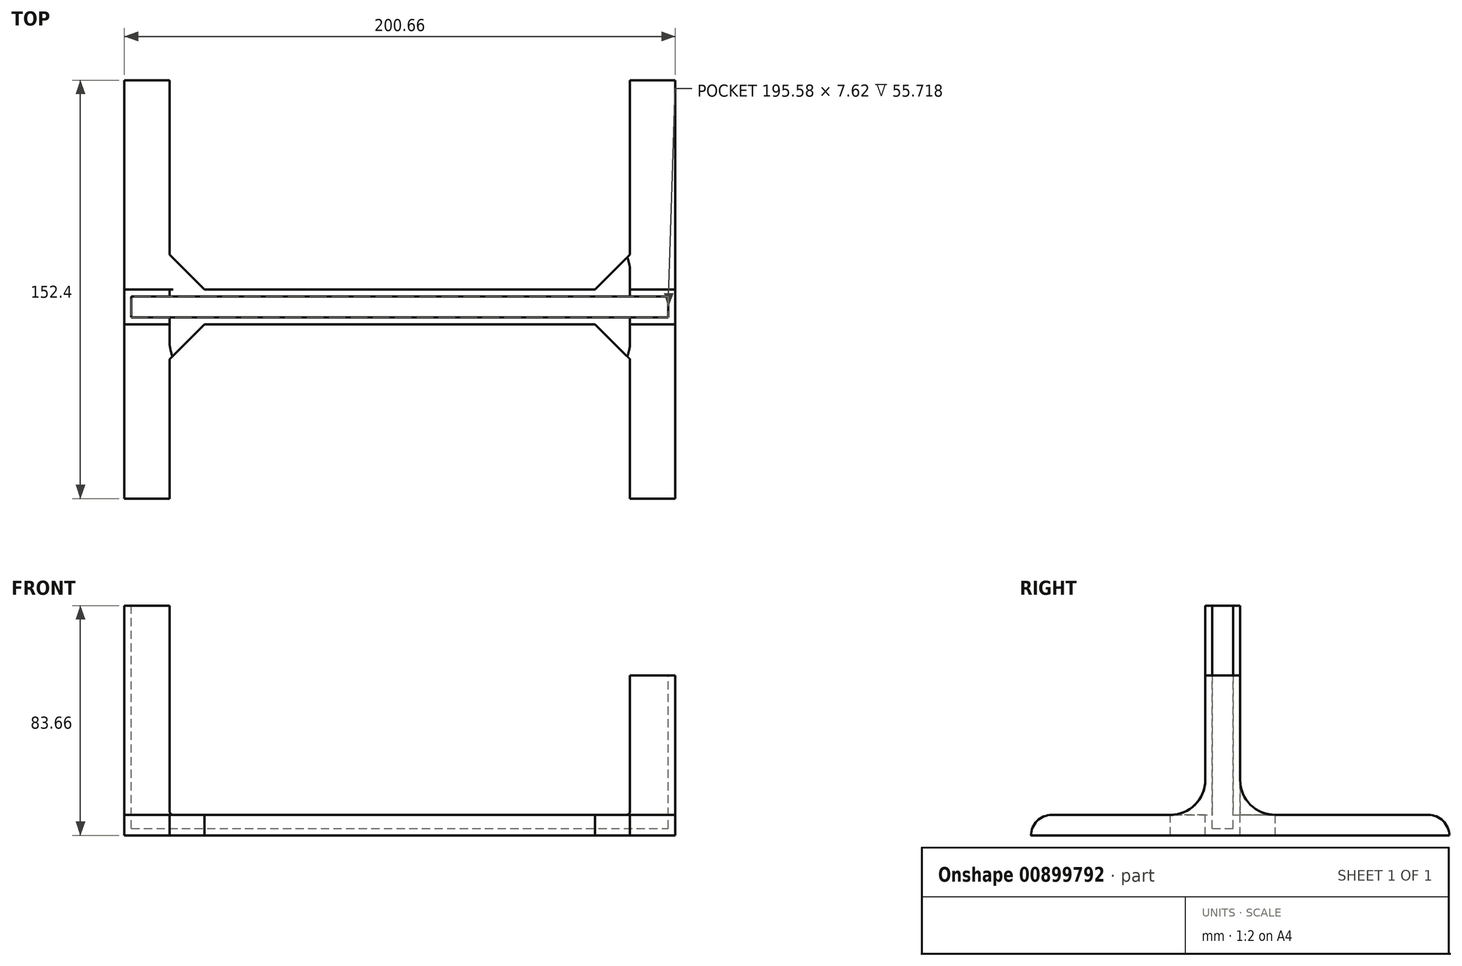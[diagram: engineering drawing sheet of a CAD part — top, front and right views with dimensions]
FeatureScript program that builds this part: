
annotation { "Feature Type Name" : "Feature", "Feature Type Description" : "" }
export const myFeature = defineFeature(function(context is Context, id is Id, definition is map)
    precondition{}
    {
        {
            var Q0;
            Q0=qCreatedBy(makeId("Front.planeOp"),FACE);
            var sketch = newSketch(context, id + "F0", { "sketchPlane" : qUnion([Q0])});
            skLineSegment(sketch, "E0.top", {"start": v(-83.82, -55.6) * mm, "end": v(83.82, -55.6) * mm});
            skLineSegment(sketch, "E0.left", {"start": v(-83.82, 55.6) * mm, "end": v(-83.82, -55.6) * mm});
            skLineSegment(sketch, "E0.right", {"start": v(83.82, 55.6) * mm, "end": v(83.82, -55.6) * mm});
            skPoint(sketch, "E0.middle", {"position": v(0, 0) * mm});
            skLineSegment(sketch, "E1", {"start": v(83.82, -55.6) * mm, "end": v(83.82, -4.8) * mm});
            skLineSegment(sketch, "E2", {"start": v(83.82, -4.8) * mm, "end": v(83.82, -55.6) * mm});
            skLineSegment(sketch, "E3", {"start": v(-83.82, -55.6) * mm, "end": v(-83.82, 20.6) * mm});
            skLineSegment(sketch, "E4.bottom", {"start": v(-100.33, -59.32) * mm, "end": v(100.33, -59.32) * mm});
            skLineSegment(sketch, "E4.left", {"start": v(-100.33, -59.32) * mm, "end": v(-100.33, 59.32) * mm});
            skLineSegment(sketch, "E4.right", {"start": v(100.33, -59.32) * mm, "end": v(100.33, 59.32) * mm});
            skLineSegment(sketch, "E5", {"start": v(-83.82, 20.6) * mm, "end": v(-100.33, 20.6) * mm});
            skLineSegment(sketch, "E6", {"start": v(-100.33, 20.6) * mm, "end": v(-83.82, 20.6) * mm});
            skLineSegment(sketch, "E7", {"start": v(83.82, -4.8) * mm, "end": v(100.33, -4.8) * mm});
            skLineSegment(sketch, "E8.top", {"start": v(-100.33, -63.05) * mm, "end": v(100.33, -63.05) * mm});
            skLineSegment(sketch, "E8.left", {"start": v(-100.33, -59.32) * mm, "end": v(-100.33, -63.05) * mm});
            skLineSegment(sketch, "E8.right", {"start": v(100.33, -59.32) * mm, "end": v(100.33, -63.05) * mm});
            skSolve(sketch);
        }
        {
            var Q0;
            {var subQ2=sQuery(id+"F0.wireOp",EDGE,"E0.top");Q0=makeQuery(id+"F0.imprint","IMPRINT",FACE,{"disambiguationData":[TD([[makeQuery(id+"F0.imprint","IMPRINT",EDGE,{"derivedFrom":subQ2}),-1.0]])]});}
            var Q1;
            Q1=makeQuery(id+"F0.imprint","IMPRINT",FACE,{"disambiguationData":[TD([[makeQuery(id+"F0.imprint","IMPRINT",EDGE,{"derivedFrom":sQuery(id+"F0.wireOp",EDGE,"E4.bottom")}),-1.0]])]});
            extrude(context, id + "F1", {"entities" : qUnion([Q0, Q1]), "depth" : 12.7 * mm, "offsetDistance" : 25.4 * mm});
        }
        {
            var Q0;
            Q0=makeQuery(id+"F1.opExtrude","SWEPT_FACE",FACE,{"disambiguationData":[OSD([sQuery(id+"F0.wireOp",EDGE,"E5")])]});
            var Q1;
            Q1=makeQuery(id+"F1.opExtrude","SWEPT_FACE",FACE,{"disambiguationData":[OSD([sQuery(id+"F0.wireOp",EDGE,"E0.left")])]});
            var Q2;
            Q2=makeQuery(id+"F1.opExtrude","SWEPT_FACE",FACE,{"disambiguationData":[OSD([sQuery(id+"F0.wireOp",EDGE,"E0.top")])]});
            var Q3;
            Q3=makeQuery(id+"F1.opExtrude","SWEPT_FACE",FACE,{"disambiguationData":[OSD([sQuery(id+"F0.wireOp",EDGE,"E7")])]});
            var Q4;
            Q4=makeQuery(id+"F1.opExtrude","SWEPT_FACE",FACE,{"disambiguationData":[OSD([sQuery(id+"F0.wireOp",EDGE,"E0.right")])]});
            shell(context, id + "F2", {"entities" : qUnion([Q0, Q1, Q2, Q3, Q4]), "thickness" : 2.54 * mm});
        }
        {
            var Q0;
            Q0=qCreatedBy(makeId("Front.planeOp"),FACE);
            var sketch = newSketch(context, id + "F3", { "sketchPlane" : qUnion([Q0])});
            skPoint(sketch, "E9.0", {"position": v(-100.33, -63.05) * mm});
            skPoint(sketch, "E10.0", {"position": v(-83.82, -55.6) * mm});
            skLineSegment(sketch, "E11.bottom", {"start": v(-83.82, -55.6) * mm, "end": v(-100.33, -55.6) * mm});
            skLineSegment(sketch, "E11.top", {"start": v(-83.82, -63.05) * mm, "end": v(-100.33, -63.05) * mm});
            skLineSegment(sketch, "E11.left", {"start": v(-83.82, -55.6) * mm, "end": v(-83.82, -63.05) * mm});
            skLineSegment(sketch, "E11.right", {"start": v(-100.33, -55.6) * mm, "end": v(-100.33, -63.05) * mm});
            skPoint(sketch, "E12.0", {"position": v(83.82, -55.6) * mm});
            skPoint(sketch, "E13.0", {"position": v(100.33, -63.05) * mm});
            skLineSegment(sketch, "E14.bottom", {"start": v(100.33, -63.05) * mm, "end": v(83.82, -63.05) * mm});
            skLineSegment(sketch, "E14.top", {"start": v(100.33, -55.6) * mm, "end": v(83.82, -55.6) * mm});
            skLineSegment(sketch, "E14.left", {"start": v(100.33, -63.05) * mm, "end": v(100.33, -55.6) * mm});
            skLineSegment(sketch, "E14.right", {"start": v(83.82, -63.05) * mm, "end": v(83.82, -55.6) * mm});
            skSolve(sketch);
        }
        {
            var Q0;
            Q0=makeQuery(id+"F3.imprint","IMPRINT",FACE,{"disambiguationData":[TD([[makeQuery(id+"F3.imprint","IMPRINT",EDGE,{"derivedFrom":sQuery(id+"F3.wireOp",EDGE,"E14.bottom")}),-1.0]])]});
            var Q1;
            Q1=makeQuery(id+"F3.imprint","IMPRINT",FACE,{"disambiguationData":[TD([[makeQuery(id+"F3.imprint","IMPRINT",EDGE,{"derivedFrom":sQuery(id+"F3.wireOp",EDGE,"E11.bottom")}),1.0]])]});
            extrude(context, id + "F4", {"entities" : qUnion([Q0, Q1]), "operationType" : NewBodyOperationType.ADD, "oppositeDirection" : true, "depth" : 76.2 * mm, "offsetDistance" : 25.4 * mm});
        }
        {
            var Q0;
            Q0=qCreatedBy(makeId("Front.planeOp"),FACE);
            var sketch = newSketch(context, id + "F5", { "sketchPlane" : qUnion([Q0])});
            skPoint(sketch, "E15.0", {"position": v(-100.33, -63.05) * mm});
            skPoint(sketch, "E16.0", {"position": v(-83.82, -55.6) * mm});
            skPoint(sketch, "E17.0", {"position": v(83.82, -55.6) * mm});
            skPoint(sketch, "E18.0", {"position": v(100.33, -63.05) * mm});
            skLineSegment(sketch, "E19.bottom", {"start": v(-83.82, -55.6) * mm, "end": v(-100.33, -55.6) * mm});
            skLineSegment(sketch, "E19.top", {"start": v(-83.82, -63.05) * mm, "end": v(-100.33, -63.05) * mm});
            skLineSegment(sketch, "E19.left", {"start": v(-83.82, -55.6) * mm, "end": v(-83.82, -63.05) * mm});
            skLineSegment(sketch, "E19.right", {"start": v(-100.33, -55.6) * mm, "end": v(-100.33, -63.05) * mm});
            skLineSegment(sketch, "E20.bottom", {"start": v(83.82, -55.6) * mm, "end": v(100.33, -55.6) * mm});
            skLineSegment(sketch, "E20.top", {"start": v(83.82, -63.05) * mm, "end": v(100.33, -63.05) * mm});
            skLineSegment(sketch, "E20.left", {"start": v(83.82, -55.6) * mm, "end": v(83.82, -63.05) * mm});
            skLineSegment(sketch, "E20.right", {"start": v(100.33, -55.6) * mm, "end": v(100.33, -63.05) * mm});
            skSolve(sketch);
        }
        {
            var Q0;
            Q0 = qSketchRegion(id + "F5", true);
            extrude(context, id + "F6", {"entities" : qUnion([Q0]), "operationType" : NewBodyOperationType.ADD, "depth" : 76.2 * mm, "offsetDistance" : 25.4 * mm, "hasSecondDirection" : true, "secondDirectionOppositeDirection" : false, "secondDirectionDepth" : 11.18 * mm});
        }
        {
            var Q0;
            Q0=makeQuery(id+"F6.boolean.opBoolean","INTERSECT",EDGE,{"derivedFrom":[makeQuery(id+"F1.opExtrude","CAP_FACE",FACE,{"disambiguationData":[OSD([sQuery(id+"F0.wireOp",EDGE,"E0.top"),sQuery(id+"F0.wireOp",EDGE,"E0.left"),sQuery(id+"F0.wireOp",EDGE,"E0.right"),sQuery(id+"F0.wireOp",EDGE,"E4.left"),sQuery(id+"F0.wireOp",EDGE,"E4.right"),sQuery(id+"F0.wireOp",EDGE,"E5"),sQuery(id+"F0.wireOp",EDGE,"E7"),sQuery(id+"F0.wireOp",EDGE,"E8.top"),sQuery(id+"F0.wireOp",EDGE,"E8.left"),sQuery(id+"F0.wireOp",EDGE,"E8.right")])],"isStart":false}),makeQuery(id+"F6.opExtrude","SWEPT_FACE",FACE,{"disambiguationData":[OSD([sQuery(id+"F5.wireOp",EDGE,"E19.left")])]})]});
            var Q1;
            Q1=makeQuery(id+"F4.opExtrude","CAP_EDGE",EDGE,{"disambiguationData":[OSD([sQuery(id+"F3.wireOp",EDGE,"E11.left")])],"isStart":true});
            var Q2;
            Q2=makeQuery(id+"F4.opExtrude","CAP_EDGE",EDGE,{"disambiguationData":[OSD([sQuery(id+"F3.wireOp",EDGE,"E14.right")])],"isStart":true});
            var Q3;
            Q3=makeQuery(id+"F6.boolean.opBoolean","INTERSECT",EDGE,{"derivedFrom":[makeQuery(id+"F1.opExtrude","CAP_FACE",FACE,{"disambiguationData":[OSD([sQuery(id+"F0.wireOp",EDGE,"E0.top"),sQuery(id+"F0.wireOp",EDGE,"E0.left"),sQuery(id+"F0.wireOp",EDGE,"E0.right"),sQuery(id+"F0.wireOp",EDGE,"E4.left"),sQuery(id+"F0.wireOp",EDGE,"E4.right"),sQuery(id+"F0.wireOp",EDGE,"E5"),sQuery(id+"F0.wireOp",EDGE,"E7"),sQuery(id+"F0.wireOp",EDGE,"E8.top"),sQuery(id+"F0.wireOp",EDGE,"E8.left"),sQuery(id+"F0.wireOp",EDGE,"E8.right")])],"isStart":false}),makeQuery(id+"F6.opExtrude","SWEPT_FACE",FACE,{"disambiguationData":[OSD([sQuery(id+"F5.wireOp",EDGE,"E20.left")])]})]});
            chamfer(context, id + "F7", {"entities" : qUnion([Q0, Q1, Q2, Q3]), "width" : 12.7 * mm, "tangentPropagation" : true});
        }
        {
            var Q0;
            Q0=makeQuery(id+"F6.boolean.opBoolean","INTERSECT",EDGE,{"derivedFrom":[makeQuery(id+"F1.opExtrude","CAP_FACE",FACE,{"disambiguationData":[OSD([sQuery(id+"F0.wireOp",EDGE,"E0.top"),sQuery(id+"F0.wireOp",EDGE,"E0.left"),sQuery(id+"F0.wireOp",EDGE,"E0.right"),sQuery(id+"F0.wireOp",EDGE,"E4.left"),sQuery(id+"F0.wireOp",EDGE,"E4.right"),sQuery(id+"F0.wireOp",EDGE,"E5"),sQuery(id+"F0.wireOp",EDGE,"E7"),sQuery(id+"F0.wireOp",EDGE,"E8.top"),sQuery(id+"F0.wireOp",EDGE,"E8.left"),sQuery(id+"F0.wireOp",EDGE,"E8.right")])],"isStart":false}),makeQuery(id+"F6.opExtrude","SWEPT_FACE",FACE,{"disambiguationData":[OSD([sQuery(id+"F5.wireOp",EDGE,"E19.bottom")])]})]});
            var Q1;
            Q1=makeQuery(id+"F6.boolean.opBoolean","INTERSECT",EDGE,{"derivedFrom":[makeQuery(id+"F1.opExtrude","CAP_FACE",FACE,{"disambiguationData":[OSD([sQuery(id+"F0.wireOp",EDGE,"E0.top"),sQuery(id+"F0.wireOp",EDGE,"E0.left"),sQuery(id+"F0.wireOp",EDGE,"E0.right"),sQuery(id+"F0.wireOp",EDGE,"E4.left"),sQuery(id+"F0.wireOp",EDGE,"E4.right"),sQuery(id+"F0.wireOp",EDGE,"E5"),sQuery(id+"F0.wireOp",EDGE,"E7"),sQuery(id+"F0.wireOp",EDGE,"E8.top"),sQuery(id+"F0.wireOp",EDGE,"E8.left"),sQuery(id+"F0.wireOp",EDGE,"E8.right")])],"isStart":false}),makeQuery(id+"F6.opExtrude","SWEPT_FACE",FACE,{"disambiguationData":[OSD([sQuery(id+"F5.wireOp",EDGE,"E20.bottom")])]})]});
            var Q2;
            Q2=makeQuery(id+"F4.opExtrude","CAP_EDGE",EDGE,{"disambiguationData":[OSD([sQuery(id+"F3.wireOp",EDGE,"E14.top")])],"isStart":true});
            var Q3;
            Q3=makeQuery(id+"F4.opExtrude","CAP_EDGE",EDGE,{"disambiguationData":[OSD([sQuery(id+"F3.wireOp",EDGE,"E11.bottom")])],"isStart":true});
            fillet(context, id + "F8", {"entities" : qUnion([Q0, Q1, Q2, Q3]), "radius" : 12.7 * mm, "tangentPropagation" : true, "allowEdgeOverflow" : false});
        }
        {
            var Q0;
            Q0=makeQuery(id+"F2.opShell","OFFSET_EDGE",EDGE,{"disambiguationData":[OSD([sQuery(id+"F0.wireOp",EDGE,"E0.top"),sQuery(id+"F0.wireOp",EDGE,"E0.left")])]});
            var Q1;
            Q1=makeQuery(id+"F1.opExtrude","SWEPT_EDGE",EDGE,{"disambiguationData":[OSD([sQuery(id+"F0.wireOp",EDGE,"E0.top"),sQuery(id+"F0.wireOp",EDGE,"E0.left")])]});
            var Q2;
            Q2=makeQuery(id+"F1.opExtrude","SWEPT_EDGE",EDGE,{"disambiguationData":[OSD([sQuery(id+"F0.wireOp",EDGE,"E0.top"),sQuery(id+"F0.wireOp",EDGE,"E0.right")])]});
            var Q3;
            Q3=makeQuery(id+"F2.opShell","OFFSET_EDGE",EDGE,{"disambiguationData":[OSD([sQuery(id+"F0.wireOp",EDGE,"E0.top"),sQuery(id+"F0.wireOp",EDGE,"E0.right")])]});
            fillet(context, id + "F9", {"entities" : qUnion([Q0, Q1, Q2, Q3]), "radius" : 1.27 * mm, "tangentPropagation" : true, "allowEdgeOverflow" : false});
        }
        {
            var Q0;
            Q0=makeQuery(id+"F4.opExtrude","CAP_EDGE",EDGE,{"disambiguationData":[OSD([sQuery(id+"F3.wireOp",EDGE,"E11.bottom")])],"isStart":false});
            var Q1;
            Q1=makeQuery(id+"F4.opExtrude","CAP_EDGE",EDGE,{"disambiguationData":[OSD([sQuery(id+"F3.wireOp",EDGE,"E14.top")])],"isStart":false});
            var Q2;
            Q2=makeQuery(id+"F6.opExtrude","CAP_EDGE",EDGE,{"disambiguationData":[OSD([sQuery(id+"F5.wireOp",EDGE,"E20.bottom")])],"isStart":false});
            var Q3;
            Q3=makeQuery(id+"F6.opExtrude","CAP_EDGE",EDGE,{"disambiguationData":[OSD([sQuery(id+"F5.wireOp",EDGE,"E19.bottom")])],"isStart":false});
            fillet(context, id + "F10", {"entities" : qUnion([Q0, Q1, Q2, Q3]), "radius" : 7.62 * mm, "tangentPropagation" : true, "allowEdgeOverflow" : false});
        }
    });
